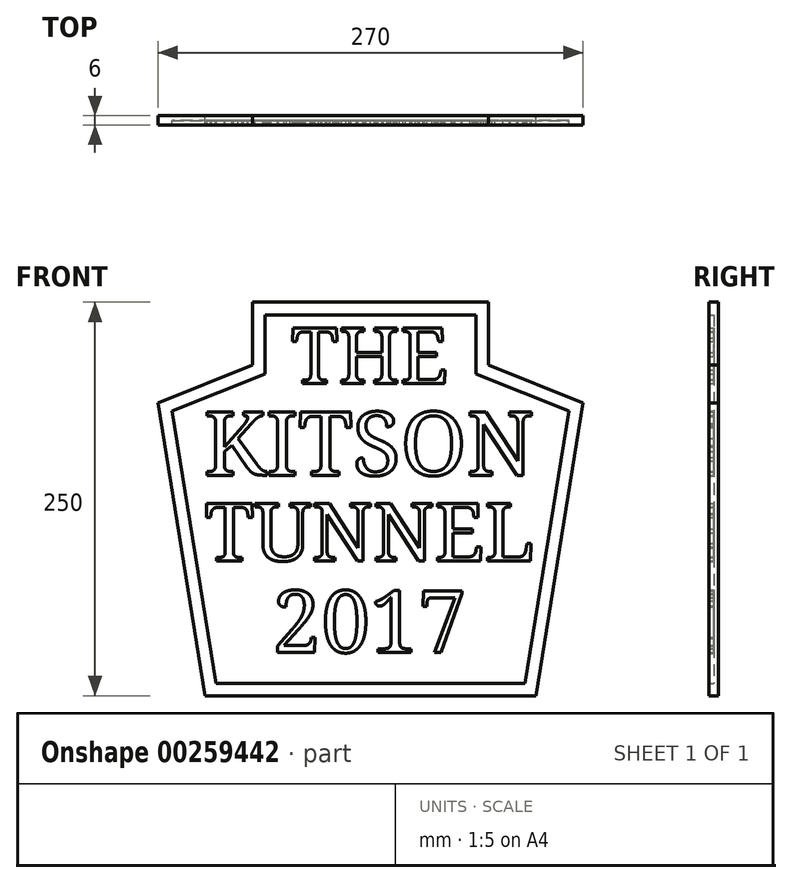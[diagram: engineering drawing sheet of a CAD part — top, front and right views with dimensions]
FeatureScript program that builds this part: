
annotation { "Feature Type Name" : "Feature", "Feature Type Description" : "" }
export const myFeature = defineFeature(function(context is Context, id is Id, definition is map)
    precondition{}
    {
        {
            var Q0;
            Q0=qCreatedBy(makeId("Front.planeOp"),FACE);
            var sketch = newSketch(context, id + "F0", { "sketchPlane" : qUnion([Q0])});
            skLineSegment(sketch, "E0", {"start": v(0, 0) * mm, "end": v(210, 0) * mm});
            skLineSegment(sketch, "E1", {"start": v(105, 0) * mm, "end": v(105, 250) * mm, "construction": true});
            skLineSegment(sketch, "E2", {"start": v(105, 250) * mm, "end": v(30, 250) * mm});
            skLineSegment(sketch, "E3", {"start": v(30, 250) * mm, "end": v(30, 210) * mm});
            skLineSegment(sketch, "E4", {"start": v(30, 210) * mm, "end": v(-30, 186.13) * mm});
            skLineSegment(sketch, "E5", {"start": v(-30, 186.13) * mm, "end": v(0, 0) * mm});
            skLineSegment(sketch, "E6.MirrorCS", {"start": v(105, 250) * mm, "end": v(180, 250) * mm});
            skLineSegment(sketch, "E7.MirrorCS", {"start": v(180, 250) * mm, "end": v(180, 210) * mm});
            skLineSegment(sketch, "E8.MirrorCS", {"start": v(180, 210) * mm, "end": v(240, 186.13) * mm});
            skLineSegment(sketch, "E9.MirrorCS", {"start": v(240, 186.13) * mm, "end": v(210, 0) * mm});
            skLineSegment(sketch, "E10", {"start": v(-30, 186.13) * mm, "end": v(105, 186.13) * mm, "construction": true});
            skSolve(sketch);
        }
        {
            var Q0;
            Q0=qSketchRegion(id+"F0",true);
            extrude(context, id + "F1", {"entities" : qUnion([Q0]), "depth" : 3 * mm});
        }
        {
            var Q0;
            Q0=makeQuery(id+"F1.opExtrude","CAP_FACE",FACE,{"disambiguationData":[OSD([sQuery(id+"F0.wireOp",EDGE,"E0"),sQuery(id+"F0.wireOp",EDGE,"E2"),sQuery(id+"F0.wireOp",EDGE,"E3"),sQuery(id+"F0.wireOp",EDGE,"E4"),sQuery(id+"F0.wireOp",EDGE,"E5"),sQuery(id+"F0.wireOp",EDGE,"E6.MirrorCS"),sQuery(id+"F0.wireOp",EDGE,"E7.MirrorCS"),sQuery(id+"F0.wireOp",EDGE,"E8.MirrorCS"),sQuery(id+"F0.wireOp",EDGE,"E9.MirrorCS")])],"isStart":false});
            var sketch = newSketch(context, id + "F2", { "sketchPlane" : qUnion([Q0])});
            skLineSegment(sketch, "E11.1", {"start": v(15, 266.6) * mm, "end": v(-15.3, 203.26) * mm, "construction": true});
            skLineSegment(sketch, "E11.3", {"start": v(-15.3, 203.26) * mm, "end": v(12.92, 15) * mm, "construction": true});
            skLineSegment(sketch, "E11.5", {"start": v(135, 266.6) * mm, "end": v(165.3, 203.26) * mm, "construction": true});
            skLineSegment(sketch, "E11.6", {"start": v(165.3, 203.26) * mm, "end": v(137.08, 15) * mm, "construction": true});
            skLineSegment(sketch, "E11.7", {"start": v(12.92, 15) * mm, "end": v(137.08, 15) * mm, "construction": true});
            skLineSegment(sketch, "E12", {"start": v(105, 250) * mm, "end": v(105, 0) * mm, "construction": true});
            skText(sketch, "E13", { "text": "KITSON", "fontName": "NotoSerif-Regular.ttf"});
            skPoint(sketch, "E14", {"position": v(302.06, 145.94) * mm});
            skText(sketch, "E15", { "text": "TUNNEL", "fontName": "NotoSerif-Regular.ttf"});
            skText(sketch, "E16", { "text": "2017", "fontName": "NotoSerif-Regular.ttf"});
            skText(sketch, "E17", { "text": "THE", "fontName": "NotoSerif-Regular.ttf"});
            const initialGuessF2  = {"E13": [-0.0009, 0.14008, 1, 0, 0.0405], "E15": [-0.00026, 0.08575, 1, 0, 0.03674], "E16": [0.04323, 0.0276, 1, 0, 0.03948], "E17": [0.05453, 0.19845, 1, 0, 0.03542]};
            skSetInitialGuess(sketch, initialGuessF2);
            skSolve(sketch);
        }
        {
            var Q0;
            Q0=qSketchRegion(id+"F2",true);
            extrude(context, id + "F3", {"entities" : qUnion([Q0]), "operationType" : NewBodyOperationType.ADD, "depth" : 3 * mm});
        }
        {
            var Q0;
            {var subQ0=sQuery(id+"F0.wireOp",EDGE,"E3");var subQ1=sQuery(id+"F0.wireOp",EDGE,"E9.MirrorCS");var subQ2=sQuery(id+"F0.wireOp",EDGE,"E8.MirrorCS");var subQ3=sQuery(id+"F0.wireOp",EDGE,"E7.MirrorCS");var subQ4=sQuery(id+"F0.wireOp",EDGE,"E5");var subQ5=sQuery(id+"F0.wireOp",EDGE,"E0");var subQ6=sQuery(id+"F0.wireOp",EDGE,"E4");var subQ7=sQuery(id+"F0.wireOp",EDGE,"E6.MirrorCS");var subQ8=sQuery(id+"F0.wireOp",EDGE,"E2");Q0=makeQuery(id+"F3.boolean.opBoolean","SPLIT",FACE,{"disambiguationData":[TD([makeQuery(id+"F1.opExtrude","SWEPT_FACE",FACE,{"disambiguationData":[OSD([subQ5])]})])],"derivedFrom":makeQuery(id+"F1.opExtrude","CAP_FACE",FACE,{"disambiguationData":[OSD([subQ5,subQ8,subQ0,subQ6,subQ4,subQ7,subQ3,subQ2,subQ1])],"isStart":false})});}
            var sketch = newSketch(context, id + "F4", { "sketchPlane" : qUnion([Q0])});
            skLineSegment(sketch, "E18.0", {"start": v(38, 242) * mm, "end": v(172, 242) * mm});
            skLineSegment(sketch, "E18.1", {"start": v(172, 242) * mm, "end": v(172, 204.57) * mm});
            skLineSegment(sketch, "E18.2", {"start": v(38, 242) * mm, "end": v(38, 204.57) * mm});
            skLineSegment(sketch, "E18.3", {"start": v(172, 204.57) * mm, "end": v(231.08, 181.07) * mm});
            skLineSegment(sketch, "E18.4", {"start": v(38, 204.57) * mm, "end": v(-21.08, 181.07) * mm});
            skLineSegment(sketch, "E18.5", {"start": v(-21.08, 181.07) * mm, "end": v(6.81, 8) * mm});
            skLineSegment(sketch, "E18.6", {"start": v(6.81, 8) * mm, "end": v(203.19, 8) * mm});
            skLineSegment(sketch, "E18.7", {"start": v(231.08, 181.07) * mm, "end": v(203.19, 8) * mm});
            skLineSegment(sketch, "E19.0", {"start": v(30, 250) * mm, "end": v(30, 210) * mm});
            skLineSegment(sketch, "E19.1", {"start": v(30, 210) * mm, "end": v(-30, 186.13) * mm});
            skLineSegment(sketch, "E19.2", {"start": v(30, 250) * mm, "end": v(180, 250) * mm});
            skLineSegment(sketch, "E19.3", {"start": v(-30, 186.13) * mm, "end": v(0, 0) * mm});
            skLineSegment(sketch, "E19.4", {"start": v(180, 250) * mm, "end": v(180, 210) * mm});
            skLineSegment(sketch, "E19.5", {"start": v(180, 210) * mm, "end": v(240, 186.13) * mm});
            skLineSegment(sketch, "E19.6", {"start": v(240, 186.13) * mm, "end": v(210, 0) * mm});
            skLineSegment(sketch, "E19.7", {"start": v(0, 0) * mm, "end": v(210, 0) * mm});
            skSolve(sketch);
        }
        {
            var Q0;
            Q0=qSketchRegion(id+"F4",true);
            extrude(context, id + "F5", {"entities" : qUnion([Q0]), "operationType" : NewBodyOperationType.ADD, "depth" : 3 * mm});
        }
    });
